# Revit family: Gas-Detectors-Transmitters_Generation-2-Remote_Brasch
name_source: partatom
category: Generic Models
units: mm (PartAtom-declared; Revit-internal decimal feet)

## family parameters
Always vertical = Yes
Can host rebar = No
Cut with Voids When Loaded = No
Maintain Annotation Orientation = No
Part Type = Normal
Room Calculation Point = No
Round Connector Dimension = Use Diameter
Shared = No
Work Plane-Based = No

## types (7) — shared parameters
CAD Details = https://www.arcat.com
DEPTH = 2.18"
Default Elevation = 0.00"
HEIGHT = 4.98"
Input Voltage = 24 VAC
Keynote = 28 42 15
Manufacturer = Brasch Environmental Technologies
Material = Gray
Product Page URL = https://www.arcat.com
Specification = https://www.arcat.com
URL = https://braschenvtech.com
WIDTH = 4.98"

## type names (no varying parameters)
- GEN2-CM-Remote, Carbon Monoxide
- GEN2-ND-Remote, Nitrogen Dioxide
- GEN2-ME-Remote, Methane
- GEN2-PR-Remote, Propane
- GEN2-HY-Remote, Hydrogen
- GEN2-OX-Remote, Oxygen
- GEN2-NCM-Remote, Carbon Monoxide and Nitrogen Dioxide

## geometry (parser evidence)
native form markers: Sweep x5
no freeform markers — native parametric forms only
